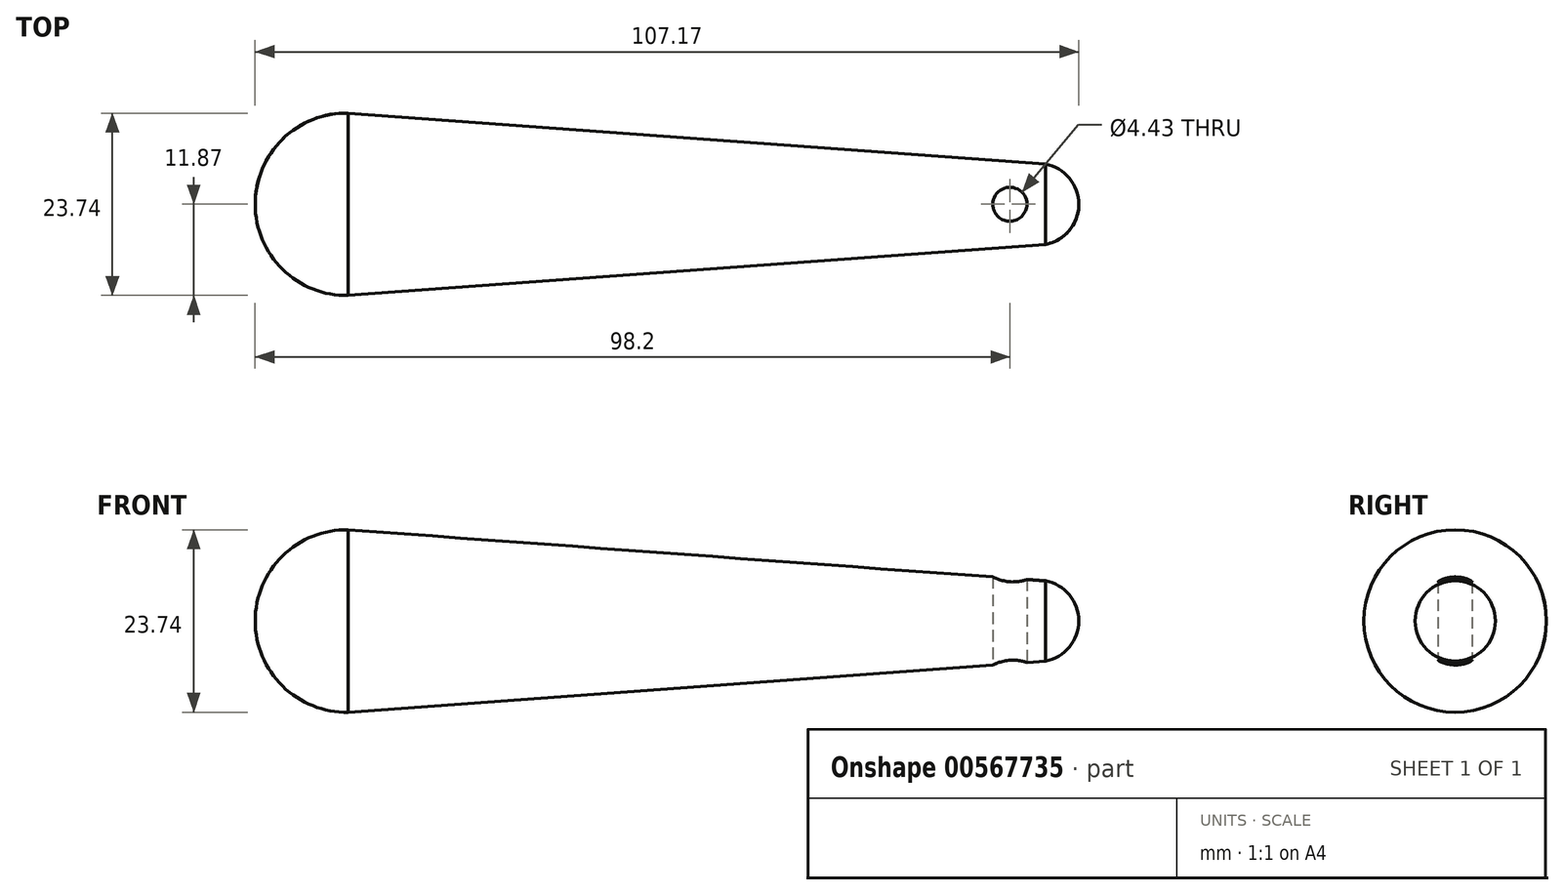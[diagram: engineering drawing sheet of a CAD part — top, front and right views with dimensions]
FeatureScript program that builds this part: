
annotation { "Feature Type Name" : "Feature", "Feature Type Description" : "" }
export const myFeature = defineFeature(function(context is Context, id is Id, definition is map)
    precondition{}
    {
        {
            var Q0;
            Q0=qCreatedBy(makeId("Top.planeOp"),FACE);
            var sketch = newSketch(context, id + "F0", { "sketchPlane" : qUnion([Q0])});
            skArc(sketch, "E0", {"start": v(-49.27, 0) * mm, "mid": v(-45.7, -8.48) * mm, "end": v(-37.16, -11.87) * mm});
            skArc(sketch, "E1", {"start": v(57.9, 0) * mm, "mid": v(56.66, -3.4) * mm, "end": v(53.54, -5.22) * mm});
            skLineSegment(sketch, "E2", {"start": v(-37.16, -11.87) * mm, "end": v(53.54, -5.22) * mm});
            skLineSegment(sketch, "E3", {"start": v(-49.27, 0) * mm, "end": v(57.9, 0) * mm});
            skSolve(sketch);
        }
        {
            var Q0;
            Q0=makeQuery(id+"F0.imprint","IMPRINT",FACE,{"disambiguationData":[TD([[makeQuery(id+"F0.imprint","IMPRINT",EDGE,{"derivedFrom":sQuery(id+"F0.wireOp",EDGE,"E0")}),1.0]])]});
            var Q1;
            Q1=sQuery(id+"F0.wireOp",EDGE,"E0");
            var Q2;
            Q2=sQuery(id+"F0.wireOp",EDGE,"E2");
            var Q3;
            Q3=sQuery(id+"F0.wireOp",EDGE,"E1");
            var Q4;
            Q4=sQuery(id+"F0.wireOp",EDGE,"E3");
            revolve(context, id + "F1", {"entities" : qUnion([Q0]), "surfaceEntities" : qUnion([Q1, Q2, Q3]), "axis" : qUnion([Q4]), "revolveType" : RevolveType.FULL});
        }
        {
            var Q0;
            Q0=qCreatedBy(makeId("Top.planeOp"),FACE);
            cPlane(context, id + "F2", {"entities" : qUnion([Q0]), "cplaneType" : CPlaneType.OFFSET, "offset" : 50.8 * mm, "oppositeDirection" : true, "width" : 152.4 * mm, "height" : 152.4 * mm});
        }
        {
            var Q0;
            Q0=qCreatedBy(id+"F2.planeOp",FACE);
            var sketch = newSketch(context, id + "F3", { "sketchPlane" : qUnion([Q0])});
            skCircle(sketch, "E4", {"center": v(48.93, 0) * mm, "radius": 2.22 * mm});
            skSolve(sketch);
        }
        {
            var Q0;
            Q0 = qSketchRegion(id + "F3", true);
            extrude(context, id + "F4", {"entities" : qUnion([Q0]), "operationType" : NewBodyOperationType.REMOVE, "endBound" : BoundingType.THROUGH_ALL, "depth" : 25.4 * mm, "offsetDistance" : 25.4 * mm});
        }
    });
